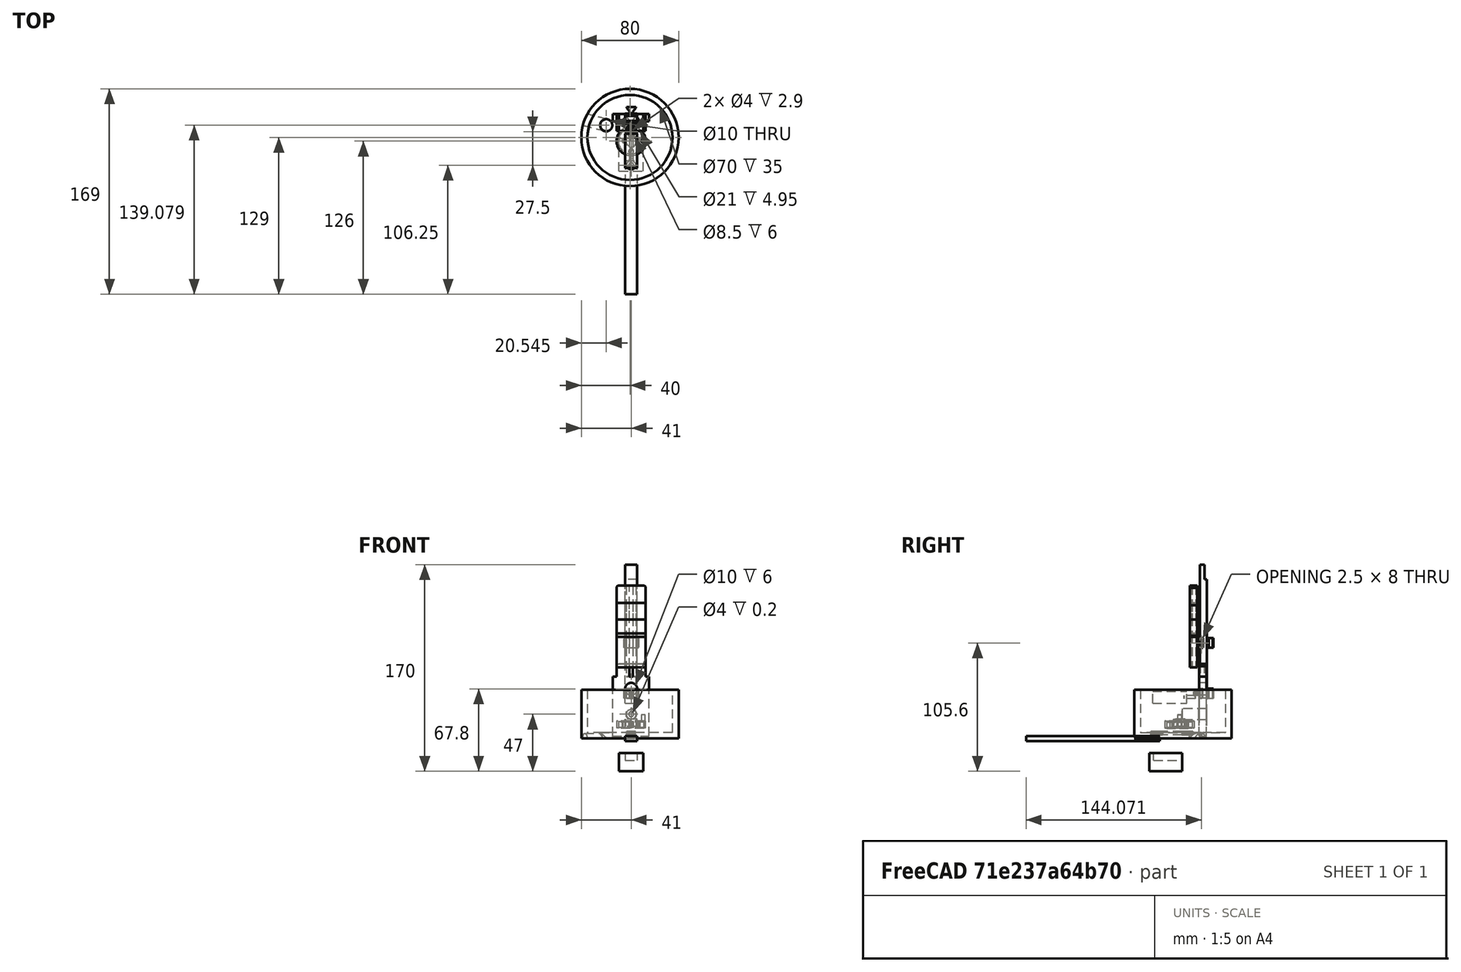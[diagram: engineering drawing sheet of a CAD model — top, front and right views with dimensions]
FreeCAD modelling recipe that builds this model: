
FCSTD DOCUMENT  (FreeCAD 1.0R39319 (Git))
Label: unicorn_lamp_gears
License: All rights reserved
LicenseURL: https://en.wikipedia.org/wiki/All_rights_reserved
objects: Part::Cylinder×24, Part::FeaturePython×14, App::Part×11, Part::Cut×11, Part::Feature×10, Part::Box×7, Part::Plane×6, Mesh::Feature×5, Part::MultiFuse×5, Part::Fuse×2, PartDesign::Body×1, PartDesign::AdditiveCylinder×1, App::DocumentObjectGroup×1
note: 83 computed .brp shape members not serialized (recipe doc carries the construction recipe); baked Part::Feature solids carry a one-line shape summary decoded from their .brp

FEATURE [Mesh::Feature] Unicorn_Lamp__3_  label="outer_mesh_with_holes"
FEATURE [PartDesign::Body] Body  label="outer_cylinder"
  AllowCompound = false
  Origin = -> Origin001
FEATURE [PartDesign::AdditiveCylinder] Cylinder
  Angle = 360
  AttacherType = Attacher::AttachEngine3D
  AttachmentSupport = -> [Origin001]
  FirstAngle = 0
  Height = 40
  Placement = pos=(-1,3,-10) rot=(0,0,1;0rad)
  Radius = 40
  Refine = true
  SecondAngle = 0
  Suppressed = false
FEATURE [Mesh::Feature] rod  label="crank_rod_mesh"
  Placement = pos=(-1.3e-15,-6,-7) rot=(0,0,-1;1.5708rad)
FEATURE [Mesh::Feature] crank_clearence_fit  label="crank_clearence_fit_mesh"
  Placement = pos=(0,16,-13) rot=(0,0,1;0rad)
FEATURE [Mesh::Feature] base  label="crank_base_mesh"
  Placement = pos=(0,0,-20) rot=(0,0,1;0rad)
FEATURE [Mesh::Feature] slider_clearence_fit  label="crank_slider_mesh"
  Placement = pos=(0,-20,-19) rot=(0,0,1;0rad)
FEATURE [Part::Box] Box001  label="crank_to_base_mount"
  AttacherType = Attacher::AttachEngine3D
  Height = 49
  Length = 30
  Placement = pos=(-15.25,16.25,-8) rot=(0,0,1;0rad)
  Width = 6
FEATURE [Part::Box] Box004  label="gear_box001"
  AttacherType = Attacher::AttachEngine3D
  Height = 10
  Length = 10
  Placement = pos=(-5,-22,19) rot=(0,0,1;0rad)
  Width = 28
FEATURE [Part::Cylinder] Cylinder002  label="shaft001"
  Angle = 360
  AttacherType = Attacher::AttachEngine3D
  FirstAngle = 0
  Height = 9
  Placement = pos=(0,4,24) rot=(1,0,0;4.71239rad)
  Radius = 1.25
  SecondAngle = 0
FEATURE [App::Part] Part002  label="motor_for_fit001"
  Group = -> [Box004,Cylinder002]
  Origin = -> Origin003
  Placement = pos=(0,6,20) rot=(0,0,1;0rad)
FEATURE [Part::Cylinder] Cylinder003
  Angle = 360
  AttacherType = Attacher::AttachEngine3D
  FirstAngle = 0
  Height = 40
  Placement = pos=(-1,3,-5) rot=(0,0,1;0rad)
  Radius = 35
  SecondAngle = 0
FEATURE [Part::Cut] Cut001  label="base_cup"
  Base = -> Cylinder
  Tool = -> Cylinder003
FEATURE [Part::Box] Box005  label="gear_box002"
  AttacherType = Attacher::AttachEngine3D
  Height = 10
  Length = 10
  Placement = pos=(-5,-24.5,16) rot=(0,0,1;0rad)
  Width = 25
FEATURE [Part::Box] Box006  label="motor_to_base_mount001"
  AttacherType = Attacher::AttachEngine3D
  Height = 15
  Length = 20
  Placement = pos=(-10,-28,7) rot=(0,0,1;0rad)
  Width = 27
FEATURE [Part::Cut] Cut002  label="motor_mount_cutout001"
  Base = -> Box006
  Placement = pos=(0,3.25,-44) rot=(0,0,1;0rad)
  Tool = -> Box005
FEATURE [App::Part] Part006  label="motor_mount001"
  Group = -> [Box006,Box005,Cut002]
  Origin = -> Origin007
  Placement = pos=(0,-6.75,32) rot=(0,0,1;0rad)
FEATURE [Part::Box] Box  label="crank_column"
  AttacherType = Attacher::AttachEngine3D
  Height = 110
  Length = 10
  Placement = pos=(-5,-16,-12) rot=(1,0,0;1.5708rad)
  Width = 4
FEATURE [App::Part] Part001  label="crank_for_fit"
  Group = -> [crank_clearence_fit,rod,base,slider_clearence_fit,Box]
  Origin = -> Origin002
  Placement = pos=(-1.8e-15,28.75,60) rot=(-1,0,0;1.5708rad)
FEATURE [App::Part] Part003  label="sub_assembly_for_fit"
  Group = -> [Part001,Part002]
  Origin = -> Origin004
  Placement = pos=(0,0,-34) rot=(0,0,1;0rad)
FEATURE [Part::Box] Box011  label="crank_column002"
  AttacherType = Attacher::AttachEngine3D
  Height = 98
  Length = 10
  Placement = pos=(-5,-16,-13.75) rot=(1,0,0;1.5708rad)
  Width = 6
FEATURE [Part::Feature] slider_clearence_fit002_solid  label="slider_clearence_fit002 (Solid)"
  shape: bbox 12 x 8 x 16.18 mm, 518 faces (baked)
FEATURE [Part::MultiFuse] Fusion  label="crank_slider_with_column_fused"
  Placement = pos=(-1.1e-15,9,7) rot=(0,-0.707107,0.707107;3.14159rad)
  Shapes = -> [slider_clearence_fit002_solid,Box011]
FEATURE [Part::Feature] base001_solid  label="crank_base_shape (Solid)"
  shape: bbox 24 x 6.2 x 50.7 mm, 492 faces (baked)
FEATURE [Part::Cylinder] Cylinder006
  Angle = 360
  AttacherType = Attacher::AttachEngine3D
  FirstAngle = 0
  Height = 20
  Placement = pos=(-20.3237,13.1165,-15.5399) rot=(-0.026127,0.061891,0.997741;6.02987rad)
  Radius = 5
  SecondAngle = 0
FEATURE [Part::Cylinder] Cylinder007
  Angle = 360
  AttacherType = Attacher::AttachEngine3D
  FirstAngle = 0
  Height = 20
  Placement = pos=(-20.4013,13.0948,-10.7906) rot=(0.120746,0.984202,0.129484;4.69816rad)
  Radius = 5
  SecondAngle = 0
FEATURE [Part::MultiFuse] Fusion002  label="power_cable_hole"
  Shapes = -> [Cylinder007,Cylinder006]
FEATURE [Part::Cut] Cut  label="base_cup_with_hole"
  Base = -> Cut001
  Tool = -> Fusion002
FEATURE [Part::Feature] crank_clearence_fit002
  Placement = pos=(0,-16,11.5) rot=(0,0,1;0rad)
  shape: bbox 24 x 23.99 x 11 mm, 1138 faces, 0 solids (baked)
FEATURE [App::Part] Part010  label="crank_with_gear_cutout"
  Origin = -> Origin012
FEATURE [Part::Cylinder] Cylinder011  label="larger_hole"
  Angle = 360
  AttacherType = Attacher::AttachEngine3D
  FirstAngle = 0
  Height = 10
  Placement = pos=(0,32.75,10) rot=(1,0,0;1.5708rad)
  Radius = 2
  SecondAngle = 0
FEATURE [Part::Cut] Cut006  label="crank_base_larger_hole"
  Base = -> base001_solid
  Placement = pos=(-6.2e-15,-6.75,0) rot=(0,0,1;0rad)
  Tool = -> Cylinder011
FEATURE [Part::Feature] rod001
  shape: bbox 7.193 x 34.54 x 2.9 mm, 772 faces, 0 solids (baked)
FEATURE [Part::Cylinder] Cylinder012
  Angle = 360
  AttacherType = Attacher::AttachEngine3D
  FirstAngle = 0
  Height = 10
  Placement = pos=(0,7.75,-7) rot=(0,0,1;0rad)
  Radius = 2
  SecondAngle = 0
FEATURE [Part::Feature] Part_solid  label="rod_bigger_holes (Solid)"
  shape: bbox 7.193 x 34.54 x 2.9 mm, 772 faces (baked)
FEATURE [Part::Cut] Cut007
  Base = -> Part_solid
  Tool = -> Cylinder012
FEATURE [Part::Cylinder] Cylinder013  label="larger_hole001"
  Angle = 360
  AttacherType = Attacher::AttachEngine3D
  FirstAngle = 0
  Height = 10
  Placement = pos=(0,32.75,10) rot=(1,0,0;1.5708rad)
  Radius = 2
  SecondAngle = 0
FEATURE [Part::Feature] base001_solid001  label="crank_base_shape (Solid)001"
  shape: bbox 24 x 6.2 x 50.7 mm, 492 faces (baked)
FEATURE [Part::Cut] Cut009  label="crank_base_larger_hole001"
  Base = -> base001_solid001
  Placement = pos=(4.6e-15,37.5,57.75) rot=(0,0,1;3.14159rad)
  Tool = -> Cylinder013
FEATURE [Part::Plane] Plane003
  AttacherType = Attacher::AttachEngine3D
  Length = 40
  Placement = pos=(-20,7,81) rot=(0,0,1;0rad)
  Width = 10
FEATURE [Part::FeaturePython] Slice003  # WARN: FeaturePython — macro-defined, semantics opaque (R4)
  Base = -> Cut009
  Mode = 1
  Tolerance = 0
  Tools = -> [Plane003]
FEATURE [Part::FeaturePython] Slice003_child1  label="Slice003.1"  # WARN: FeaturePython — macro-defined, semantics opaque (R4)
  Base = -> Slice003
  FilterType = 1
  Invert = false
  OverrideMaxVal = 0
  Placement = pos=(0,0,-32.5) rot=(0,0,1;0rad)
  WindowFrom = 80
  WindowTo = 100
  items = 1
FEATURE [Part::Cylinder] Cylinder014  label="larger_hole002"
  Angle = 360
  AttacherType = Attacher::AttachEngine3D
  FirstAngle = 0
  Height = 10
  Placement = pos=(0,32.75,10) rot=(1,0,0;1.5708rad)
  Radius = 2
  SecondAngle = 0
FEATURE [Part::Plane] Plane004
  AttacherType = Attacher::AttachEngine3D
  Length = 40
  Placement = pos=(-20,7,81) rot=(0,0,1;0rad)
  Width = 10
FEATURE [Part::Feature] base001_solid002  label="crank_base_shape (Solid)002"
  shape: bbox 24 x 6.2 x 50.7 mm, 492 faces (baked)
FEATURE [Part::Cut] Cut010  label="crank_base_larger_hole002"
  Base = -> base001_solid002
  Placement = pos=(4.6e-15,37.5,57.75) rot=(0,0,1;3.14159rad)
  Tool = -> Cylinder014
FEATURE [Part::FeaturePython] Slice004  # WARN: FeaturePython — macro-defined, semantics opaque (R4)
  Base = -> Cut010
  Mode = 1
  Tolerance = 0
  Tools = -> [Plane004]
FEATURE [Part::FeaturePython] Slice003_child002  label="Slice003.002"  # WARN: FeaturePython — macro-defined, semantics opaque (R4)
  Base = -> Slice004
  FilterType = 1
  Invert = false
  OverrideMaxVal = 0
  Placement = pos=(0,0,-7.5) rot=(0,0,1;0rad)
  WindowFrom = 80
  WindowTo = 100
  items = 1
FEATURE [Part::Cylinder] Cylinder018  label="larger_hole006"
  Angle = 360
  AttacherType = Attacher::AttachEngine3D
  FirstAngle = 0
  Height = 10
  Placement = pos=(0,32.75,10) rot=(1,0,0;1.5708rad)
  Radius = 2
  SecondAngle = 0
FEATURE [Part::Plane] Plane008
  AttacherType = Attacher::AttachEngine3D
  Length = 40
  Placement = pos=(-20,7,81) rot=(0,0,1;0rad)
  Width = 10
FEATURE [Part::Feature] base001_solid006  label="crank_base_shape (Solid)006"
  shape: bbox 24 x 6.2 x 50.7 mm, 492 faces (baked)
FEATURE [Part::Cut] Cut012  label="crank_base_larger_hole004"
  Base = -> base001_solid006
  Placement = pos=(4.6e-15,37.5,57.75) rot=(0,0,1;3.14159rad)
  Tool = -> Cylinder018
FEATURE [Part::FeaturePython] Slice006  # WARN: FeaturePython — macro-defined, semantics opaque (R4)
  Base = -> Cut012
  Mode = 1
  Tolerance = 0
  Tools = -> [Plane008]
FEATURE [Part::FeaturePython] Slice003_child004  label="Slice003.004"  # WARN: FeaturePython — macro-defined, semantics opaque (R4)
  Base = -> Slice006
  FilterType = 1
  Invert = false
  OverrideMaxVal = 0
  Placement = pos=(0,0,6.75) rot=(0,0,1;0rad)
  WindowFrom = 80
  WindowTo = 100
  items = 1
FEATURE [Part::Feature] slider_clearence_fit002_solid001  label="slider_clearence_fit002 (Solid)001"
  Placement = pos=(0,9,88.6) rot=(1,0,0;1.5708rad)
  shape: bbox 12 x 16.18 x 8 mm, 518 faces (baked)
FEATURE [Part::Fuse] Fusion004
  Base = -> Fusion
  Tool = -> slider_clearence_fit002_solid001
FEATURE [Part::Plane] Plane009
  AttacherType = Attacher::AttachEngine3D
  Length = 10
  Placement = pos=(-5,16.75,51.6) rot=(-1,0,0;4.71239rad)
  Width = 50
FEATURE [Part::FeaturePython] Slice007  # WARN: FeaturePython — macro-defined, semantics opaque (R4)
  Base = -> Fusion004
  Mode = 1
  Tolerance = 0
  Tools = -> [Plane009]
FEATURE [Part::FeaturePython] Slice007_child0  label="slider_double_support_final"  # WARN: FeaturePython — macro-defined, semantics opaque (R4)
  Base = -> Slice007
  FilterType = 1
  Invert = false
  OverrideMaxVal = 0
  WindowFrom = 80
  WindowTo = 100
  items = 0
FEATURE [Part::Box] Box012  label="Cube"
  AttacherType = Attacher::AttachEngine3D
  Height = 15
  Length = 10
  Placement = pos=(-5,16.75,118) rot=(0,0,1;0rad)
  Width = 4
FEATURE [Part::Fuse] Fusion005
  Base = -> Slice007_child0
  Tool = -> Box012
FEATURE [App::Part] Part011  label="slider_double_support"
  Group = -> [Box011,slider_clearence_fit002_solid,Fusion,slider_clearence_fit002_solid001,Fusion004,Plane009,Slice007,Slice007_child0,Box012,Fusion005]
  Origin = -> Origin013
FEATURE [Part::Cylinder] Cylinder019
  Angle = 360
  AttacherType = Attacher::AttachEngine3D
  FirstAngle = 0
  Height = 20
  Placement = pos=(0,2.25,10) rot=(-1,0,0;1.5708rad)
  Radius = 4.5
  SecondAngle = 0
FEATURE [Part::Cylinder] Cylinder020
  Angle = 360
  AttacherType = Attacher::AttachEngine3D
  FirstAngle = 0
  Height = 20
  Placement = pos=(0,9.75,30.8) rot=(-1,0,0;1.5708rad)
  Radius = 5
  SecondAngle = 0
FEATURE [Part::MultiFuse] Fusion006
  Shapes = -> [Cut006,Box001]
FEATURE [Part::Cut] Cut013
  Base = -> Fusion006
  Tool = -> Cylinder020
FEATURE [App::Part] Part005  label="crank_mount"
  Group = -> [Box001,base001_solid,Cylinder011,Cut006,Cylinder020,Fusion006,Cut013]
  Origin = -> Origin006
  Placement = pos=(3.8e-15,30.75,0) rot=(0,0,1;3.14159rad)
FEATURE [App::Part] Part004  label="lamp_base"
  Group = -> [Body,Part005,Part006,Cylinder006,Cylinder,Cylinder003,Cut001,Fusion002,Cylinder007,Cut,Slice003,Cylinder013,Cut009,base001_solid001,Plane003,Slice003_child1,Plane004,base001_solid002,Cut010,Cylinder014,Slice004,Slice003_child004,Slice003_child002,base001_solid006,Cut012,Slice006,Cylinder018,Plane008]
  Origin = -> Origin005
FEATURE [Part::Cylinder] Cylinder021
  Angle = 360
  AttacherType = Attacher::AttachEngine3D
  FirstAngle = 0
  Height = 6
  Placement = pos=(0,0,-1.5) rot=(0,0,1;0rad)
  Radius = 10.5
  SecondAngle = 0
FEATURE [Part::Plane] Plane
  AttacherType = Attacher::AttachEngine3D
  Length = 10
  Placement = pos=(5,-5,4.55) rot=(0,0,1;0rad)
  Width = 10
FEATURE [Part::FeaturePython] Slice  # WARN: FeaturePython — macro-defined, semantics opaque (R4)
  Base = -> crank_clearence_fit002
  Mode = 1
  Tolerance = 0
  Tools = -> [Plane]
FEATURE [Part::FeaturePython] Slice_child0  label="Slice.0"  # WARN: FeaturePython — macro-defined, semantics opaque (R4)
  Base = -> Slice
  FilterType = 1
  Invert = false
  OverrideMaxVal = 0
  WindowFrom = 80
  WindowTo = 100
  items = 0
FEATURE [Part::FeaturePython] Slice_child1  label="Slice.1"  # WARN: FeaturePython — macro-defined, semantics opaque (R4)
  Base = -> Slice
  FilterType = 1
  Invert = false
  OverrideMaxVal = 0
  Placement = pos=(0,0,-0.05) rot=(0,0,1;0rad)
  WindowFrom = 80
  WindowTo = 100
  items = 1
FEATURE [App::DocumentObjectGroup] GrExplode_Slice  label="Exploded Slice"
  Group = -> [Slice_child0,Slice_child1]
FEATURE [Part::Cylinder] Cylinder022
  Angle = 360
  AttacherType = Attacher::AttachEngine3D
  FirstAngle = 0
  Height = 6
  Placement = pos=(0,0,-1.45) rot=(0,0,1;0rad)
  Radius = 12
  SecondAngle = 0
FEATURE [Part::Plane] Plane010
  AttacherType = Attacher::AttachEngine3D
  Length = 10
  Placement = pos=(5,-5,4.55) rot=(0,0,1;0rad)
  Width = 10
FEATURE [Part::Feature] crank_clearence_fit003
  Placement = pos=(0,-16,11.5) rot=(0,0,1;0rad)
  shape: bbox 24 x 23.99 x 11 mm, 1138 faces, 0 solids (baked)
FEATURE [Part::FeaturePython] Slice008  # WARN: FeaturePython — macro-defined, semantics opaque (R4)
  Base = -> crank_clearence_fit003
  Mode = 1
  Tolerance = 0
  Tools = -> [Plane010]
FEATURE [Part::FeaturePython] Slice_child002  label="Slice.002"  # WARN: FeaturePython — macro-defined, semantics opaque (R4)
  Base = -> Slice008
  FilterType = 1
  Invert = false
  OverrideMaxVal = 0
  Placement = pos=(0,0,-0.05) rot=(0,0,1;0rad)
  WindowFrom = 80
  WindowTo = 100
  items = 1
FEATURE [Part::Cylinder] Cylinder023
  Angle = 360
  AttacherType = Attacher::AttachEngine3D
  FirstAngle = 0
  Height = 5
  Placement = pos=(0,0,-1.5) rot=(0,0,1;0rad)
  Radius = 10.5
  SecondAngle = 0
FEATURE [Part::Cut] Cut014
  Base = -> Cylinder022
  Tool = -> Cylinder023
FEATURE [Part::Cylinder] Cylinder024
  Angle = 360
  AttacherType = Attacher::AttachEngine3D
  FirstAngle = 0
  Height = 4.8
  Placement = pos=(0,6.3,-1) rot=(0,0,1;0rad)
  Radius = 1.2
  SecondAngle = 0
FEATURE [Part::Cylinder] Cylinder025
  Angle = 360
  AttacherType = Attacher::AttachEngine3D
  FirstAngle = 0
  Height = 4.8
  Placement = pos=(0,8.45,-1) rot=(0,0,1;0rad)
  Radius = 2
  SecondAngle = 0
FEATURE [Part::Cylinder] Cylinder026
  Angle = 360
  AttacherType = Attacher::AttachEngine3D
  FirstAngle = 0
  Height = 4.8
  Placement = pos=(0,-6.8,-1) rot=(0,0,1;0rad)
  Radius = 1.2
  SecondAngle = 0
FEATURE [Part::Cylinder] Cylinder027
  Angle = 360
  AttacherType = Attacher::AttachEngine3D
  FirstAngle = 0
  Height = 4.8
  Placement = pos=(0,-8.45,-1) rot=(0,0,1;0rad)
  Radius = 2
  SecondAngle = 0
FEATURE [Part::Cylinder] Cylinder028
  Angle = 360
  AttacherType = Attacher::AttachEngine3D
  FirstAngle = 0
  Height = 4.8
  Placement = pos=(6.3033,-0.00330086,-1) rot=(0,0,1;0rad)
  Radius = 1.2
  SecondAngle = 0
FEATURE [Part::Cylinder] Cylinder029
  Angle = 360
  AttacherType = Attacher::AttachEngine3D
  FirstAngle = 0
  Height = 4.8
  Placement = pos=(-8.51472,-0.0352814,-1) rot=(0,0,1;0rad)
  Radius = 2
  SecondAngle = 0
FEATURE [Part::Cylinder] Cylinder030
  Angle = 360
  AttacherType = Attacher::AttachEngine3D
  FirstAngle = 0
  Height = 4.8
  Placement = pos=(8.48528,-0.0352814,-1) rot=(0,0,1;5.49779rad)
  Radius = 2
  SecondAngle = 0
FEATURE [Part::Cylinder] Cylinder031
  Angle = 360
  AttacherType = Attacher::AttachEngine3D
  FirstAngle = 0
  Height = 4.8
  Placement = pos=(-6.2967,-0.00330086,-1) rot=(0,0,1;0rad)
  Radius = 1.2
  SecondAngle = 0
FEATURE [Part::MultiFuse] Fusion007
  Shapes = -> [Cut014,Cylinder026,Cylinder028,Cylinder024,Cylinder031]
FEATURE [Part::Cylinder] Cylinder032
  Angle = 360
  AttacherType = Attacher::AttachEngine3D
  FirstAngle = 0
  Height = 5.2
  Placement = pos=(10,0,4.3) rot=(0,0,1;0rad)
  Radius = 1.5
  SecondAngle = 0
FEATURE [Part::MultiFuse] Fusion008
  Shapes = -> [Fusion007,Cylinder032]
FEATURE [App::Part] Part012  label="crank_for_gear"
  Group = -> [Plane010,crank_clearence_fit003,Slice008,Slice_child002,Cylinder024,Cut014,Cylinder023,Fusion007,Cylinder028,Cylinder031,Cylinder022,Cylinder032,Cylinder026,Fusion008]
  Origin = -> Origin014
  Placement = pos=(0,0,0.8) rot=(0,0,1;0rad)
FEATURE [Part::Cylinder] Cylinder033
  Angle = 360
  AttacherType = Attacher::AttachEngine3D
  FirstAngle = 0
  Height = 10
  Placement = pos=(0,-19.75,-7) rot=(0,0,1;0rad)
  Radius = 2
  SecondAngle = 0
FEATURE [Part::Cut] Cut015
  Base = -> Cut007
  Tool = -> Cylinder033
FEATURE [App::Part] Part  label="rod_bigger_holes"
  Group = -> [rod001,Cylinder033,Cylinder012,Part_solid,Cut007,Cut015]
  Origin = -> Origin
FEATURE [Part::FeaturePython] Tube  # WARN: FeaturePython — macro-defined, semantics opaque (R4)
  AttacherType = Attacher::AttachEngine3D
  Height = 6
  InnerRadius = 4.25
  OuterRadius = 4.85
FEATURE [App::Part] Part013  label="resize_hole"
  Group = -> [Tube,Cylinder030]
  Origin = -> Origin015
